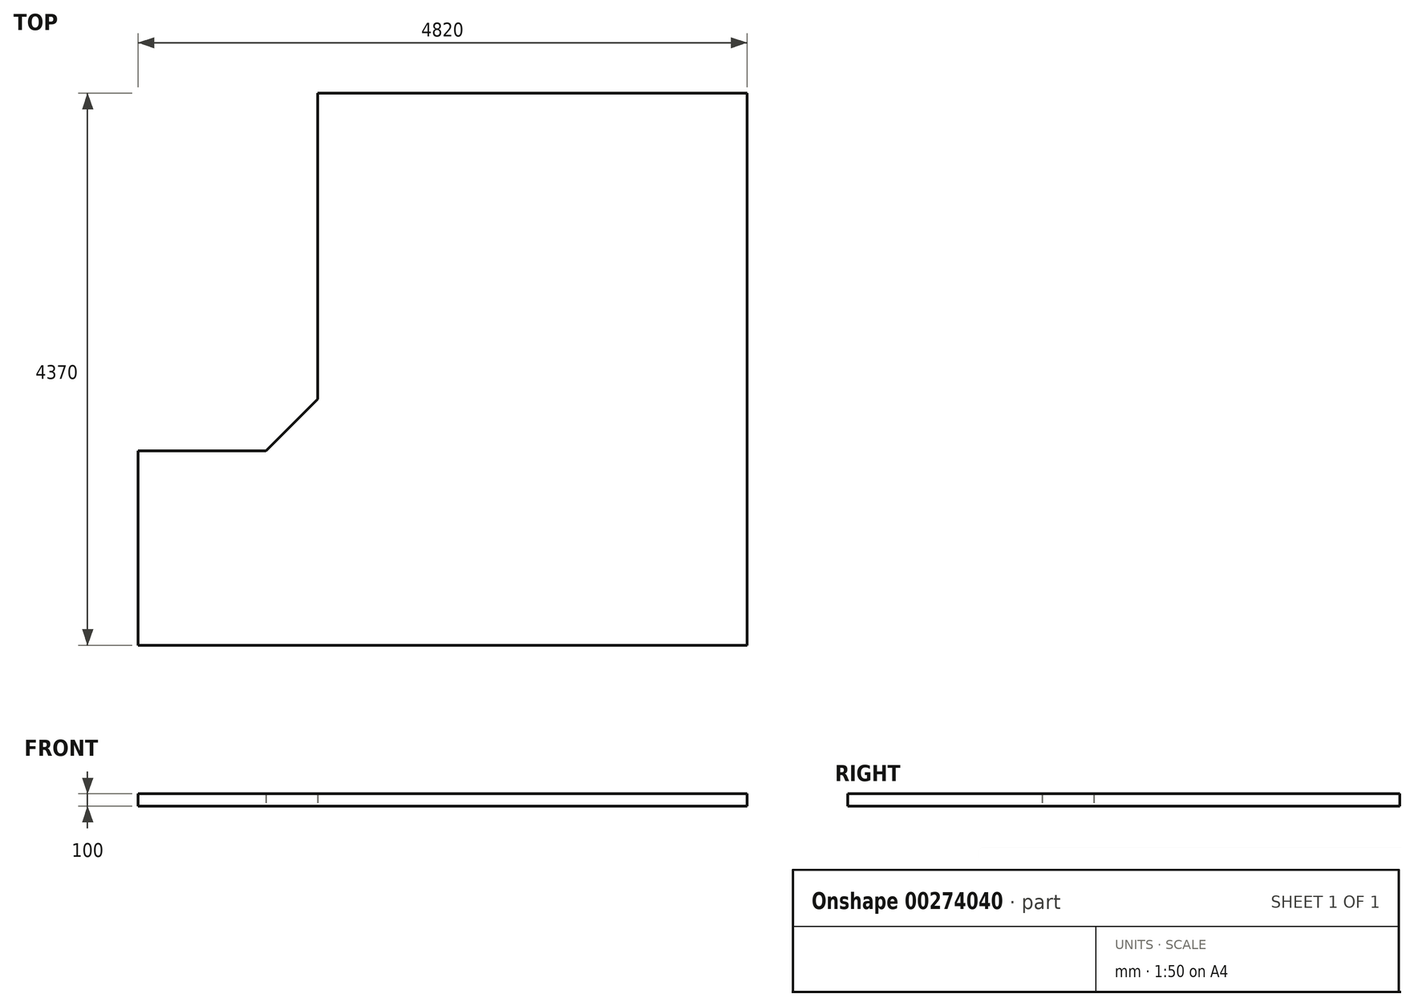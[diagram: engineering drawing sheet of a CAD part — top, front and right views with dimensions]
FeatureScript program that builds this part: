
annotation { "Feature Type Name" : "Feature", "Feature Type Description" : "" }
export const myFeature = defineFeature(function(context is Context, id is Id, definition is map)
    precondition{}
    {
        {
            var Q0;
            Q0=qCreatedBy(makeId("Top.planeOp"),FACE);
            var sketch = newSketch(context, id + "F0", { "sketchPlane" : qUnion([Q0])});
            skLineSegment(sketch, "E0", {"start": v(-2410, -1135) * mm, "end": v(-2410, -2675) * mm});
            skLineSegment(sketch, "E1", {"start": v(-2410, -2675) * mm, "end": v(2410, -2675) * mm});
            skLineSegment(sketch, "E2", {"start": v(2410, -2675) * mm, "end": v(2410, 1695) * mm});
            skLineSegment(sketch, "E3", {"start": v(2410, 1695) * mm, "end": v(-990, 1695) * mm});
            skLineSegment(sketch, "E4", {"start": v(-990, 1695) * mm, "end": v(-990, -725.9) * mm});
            skLineSegment(sketch, "E5", {"start": v(-990, -725.9) * mm, "end": v(-1399.1, -1135) * mm});
            skLineSegment(sketch, "E6", {"start": v(-1399.1, -1135) * mm, "end": v(-2410, -1135) * mm});
            skSolve(sketch);
        }
        {
            var Q0;
            Q0 = qSketchRegion(id + "F0", true);
            extrude(context, id + "F1", {"entities" : qUnion([Q0]), "depth" : 100 * mm});
        }
    });
